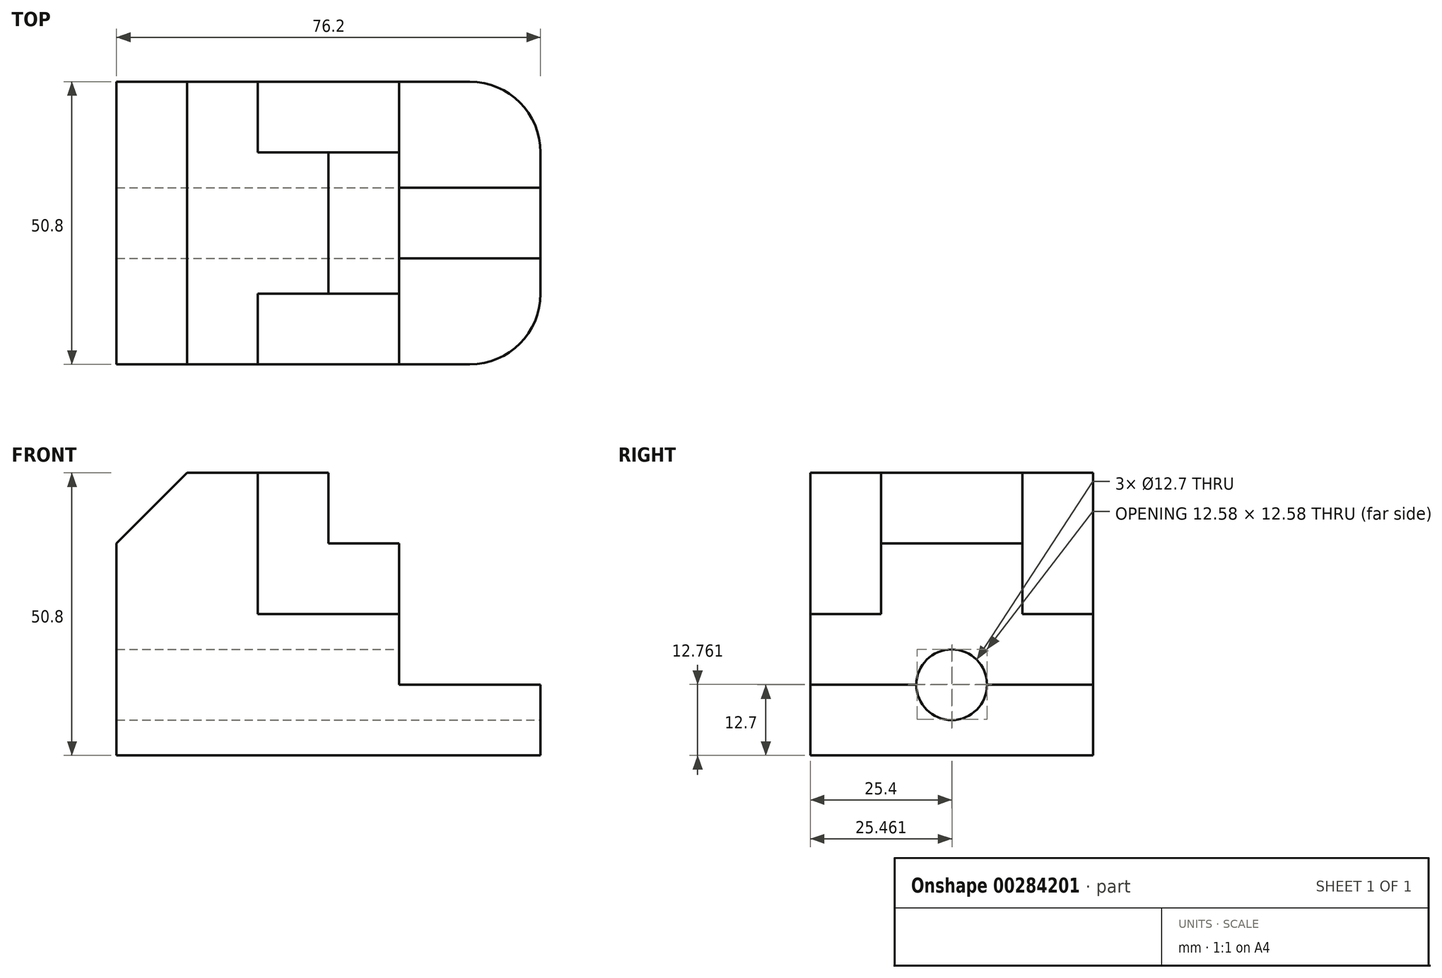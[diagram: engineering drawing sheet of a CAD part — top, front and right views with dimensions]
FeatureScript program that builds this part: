
annotation { "Feature Type Name" : "Feature", "Feature Type Description" : "" }
export const myFeature = defineFeature(function(context is Context, id is Id, definition is map)
    precondition{}
    {
        {
            var Q0;
            Q0=qCreatedBy(makeId("Front.planeOp"),FACE);
            var sketch = newSketch(context, id + "F0", { "sketchPlane" : qUnion([Q0])});
            skLineSegment(sketch, "E0", {"start": v(0, 0) * mm, "end": v(0, 38.1) * mm});
            skLineSegment(sketch, "E1", {"start": v(0, 38.1) * mm, "end": v(12.7, 50.8) * mm});
            skLineSegment(sketch, "E2", {"start": v(12.7, 50.8) * mm, "end": v(38.1, 50.8) * mm});
            skLineSegment(sketch, "E3", {"start": v(38.1, 50.8) * mm, "end": v(38.1, 38.1) * mm});
            skLineSegment(sketch, "E4", {"start": v(38.1, 38.1) * mm, "end": v(50.8, 38.1) * mm});
            skLineSegment(sketch, "E5", {"start": v(50.8, 38.1) * mm, "end": v(50.8, 12.7) * mm});
            skLineSegment(sketch, "E6", {"start": v(50.8, 12.7) * mm, "end": v(76.2, 12.7) * mm});
            skLineSegment(sketch, "E7", {"start": v(76.2, 12.7) * mm, "end": v(76.2, 0) * mm});
            skLineSegment(sketch, "E8", {"start": v(76.2, 0) * mm, "end": v(0, 0) * mm});
            skSolve(sketch);
        }
        {
            var Q0;
            Q0=makeQuery(id+"F0.imprint","IMPRINT",FACE,{"disambiguationData":[TD([[makeQuery(id+"F0.imprint","IMPRINT",EDGE,{"derivedFrom":sQuery(id+"F0.wireOp",EDGE,"E0")}),-1.0]])]});
            extrude(context, id + "F1", {"entities" : qUnion([Q0]), "depth" : 50.8 * mm});
        }
        {
            var Q0;
            Q0=makeQuery(id+"F1.opExtrude","SWEPT_FACE",FACE,{"disambiguationData":[OSD([sQuery(id+"F0.wireOp",EDGE,"E5")])]});
            var sketch = newSketch(context, id + "F2", { "sketchPlane" : qUnion([Q0])});
            skLineSegment(sketch, "E9", {"start": v(-50.8, 25.4) * mm, "end": v(-50.8, 50.8) * mm});
            skLineSegment(sketch, "E10", {"start": v(-50.8, 50.8) * mm, "end": v(-38.1, 50.8) * mm});
            skLineSegment(sketch, "E11", {"start": v(-38.1, 50.8) * mm, "end": v(-38.1, 25.4) * mm});
            skLineSegment(sketch, "E12", {"start": v(-38.1, 25.4) * mm, "end": v(-50.8, 25.4) * mm});
            skSolve(sketch);
        }
        {
            var Q0;
            Q0 = qSketchRegion(id + "F2", true);
            extrude(context, id + "F3", {"entities" : qUnion([Q0]), "operationType" : NewBodyOperationType.REMOVE, "oppositeDirection" : true, "depth" : 25.4 * mm});
        }
        {
            var Q0;
            Q0=makeQuery(id+"F1.opExtrude","SWEPT_FACE",FACE,{"disambiguationData":[OSD([sQuery(id+"F0.wireOp",EDGE,"E5")])]});
            var sketch = newSketch(context, id + "F4", { "sketchPlane" : qUnion([Q0])});
            skLineSegment(sketch, "E13", {"start": v(0, 25.4) * mm, "end": v(0, 50.8) * mm});
            skPoint(sketch, "E13.endSnap0", {"position": v(0, 25.4) * mm});
            skLineSegment(sketch, "E14", {"start": v(0, 50.8) * mm, "end": v(-12.7, 50.8) * mm});
            skLineSegment(sketch, "E15", {"start": v(-12.7, 50.8) * mm, "end": v(-12.7, 25.4) * mm});
            skLineSegment(sketch, "E16", {"start": v(-12.7, 25.4) * mm, "end": v(0, 25.4) * mm});
            skSolve(sketch);
        }
        {
            var Q0;
            {var subQ4=sQuery(id+"F4.wireOp",EDGE,"E16");Q0=makeQuery(id+"F4.imprint","IMPRINT",FACE,{"disambiguationData":[TD([[makeQuery(id+"F4.imprint","IMPRINT",EDGE,{"derivedFrom":subQ4}),1.0]])]});}
            var Q1;
            {var subQ3=sQuery(id+"F4.wireOp",EDGE,"E14");Q1=makeQuery(id+"F4.imprint","IMPRINT",FACE,{"disambiguationData":[TD([[makeQuery(id+"F4.imprint","IMPRINT",EDGE,{"derivedFrom":subQ3}),1.0]])]});}
            extrude(context, id + "F5", {"entities" : qUnion([Q0, Q1]), "operationType" : NewBodyOperationType.REMOVE, "oppositeDirection" : true, "depth" : 25.4 * mm});
        }
        {
            var Q0;
            Q0=makeQuery(id+"F1.opExtrude","SWEPT_FACE",FACE,{"disambiguationData":[OSD([sQuery(id+"F0.wireOp",EDGE,"E7")])]});
            var sketch = newSketch(context, id + "F6", { "sketchPlane" : qUnion([Q0])});
            skCircle(sketch, "E17", {"center": v(-25.4, 12.7) * mm, "radius": 6.35 * mm});
            skSolve(sketch);
        }
        {
            var Q0;
            {var subQ0=sQuery(id+"F6.wireOp",EDGE,"E17");var subQ1=makeQuery(id+"F1.opExtrude","SWEPT_EDGE",EDGE,{"disambiguationData":[OSD([sQuery(id+"F0.wireOp",EDGE,"E6"),sQuery(id+"F0.wireOp",EDGE,"E7")])]});var subQ2=makeQuery(id+"F6.imprint","INTERSECT",VERTEX,{"disambiguationData":[OD(0.0)],"derivedFrom":[subQ1,subQ0]});Q0=makeQuery(id+"F6.imprint","IMPRINT",FACE,{"disambiguationData":[TD([[makeQuery(id+"F6.imprint","IMPRINT",EDGE,{"disambiguationData":[TD([[subQ2,1.0]])],"derivedFrom":subQ0}),1.0]])]});}
            var Q1;
            {var subQ0=sQuery(id+"F6.wireOp",EDGE,"E17");var subQ1=makeQuery(id+"F1.opExtrude","SWEPT_EDGE",EDGE,{"disambiguationData":[OSD([sQuery(id+"F0.wireOp",EDGE,"E6"),sQuery(id+"F0.wireOp",EDGE,"E7")])]});var subQ2=makeQuery(id+"F6.imprint","INTERSECT",VERTEX,{"disambiguationData":[OD(0.0)],"derivedFrom":[subQ1,subQ0]});Q1=makeQuery(id+"F6.imprint","IMPRINT",FACE,{"disambiguationData":[TD([[makeQuery(id+"F6.imprint","IMPRINT",EDGE,{"disambiguationData":[TD([[subQ2,-1.0]])],"derivedFrom":subQ0}),1.0]])]});}
            extrude(context, id + "F7", {"entities" : qUnion([Q0, Q1]), "operationType" : NewBodyOperationType.REMOVE, "endBound" : BoundingType.THROUGH_ALL, "oppositeDirection" : true, "depth" : 25.4 * mm});
        }
        {
            var Q0;
            Q0=makeQuery(id+"F1.opExtrude","CAP_EDGE",EDGE,{"disambiguationData":[OSD([sQuery(id+"F0.wireOp",EDGE,"E7")])],"isStart":false});
            var Q1;
            Q1=makeQuery(id+"F1.opExtrude","CAP_EDGE",EDGE,{"disambiguationData":[OSD([sQuery(id+"F0.wireOp",EDGE,"E7")])],"isStart":true});
            fillet(context, id + "F8", {"entities" : qUnion([Q0, Q1]), "radius" : 12.7 * mm, "tangentPropagation" : true, "allowEdgeOverflow" : false});
        }
    });
